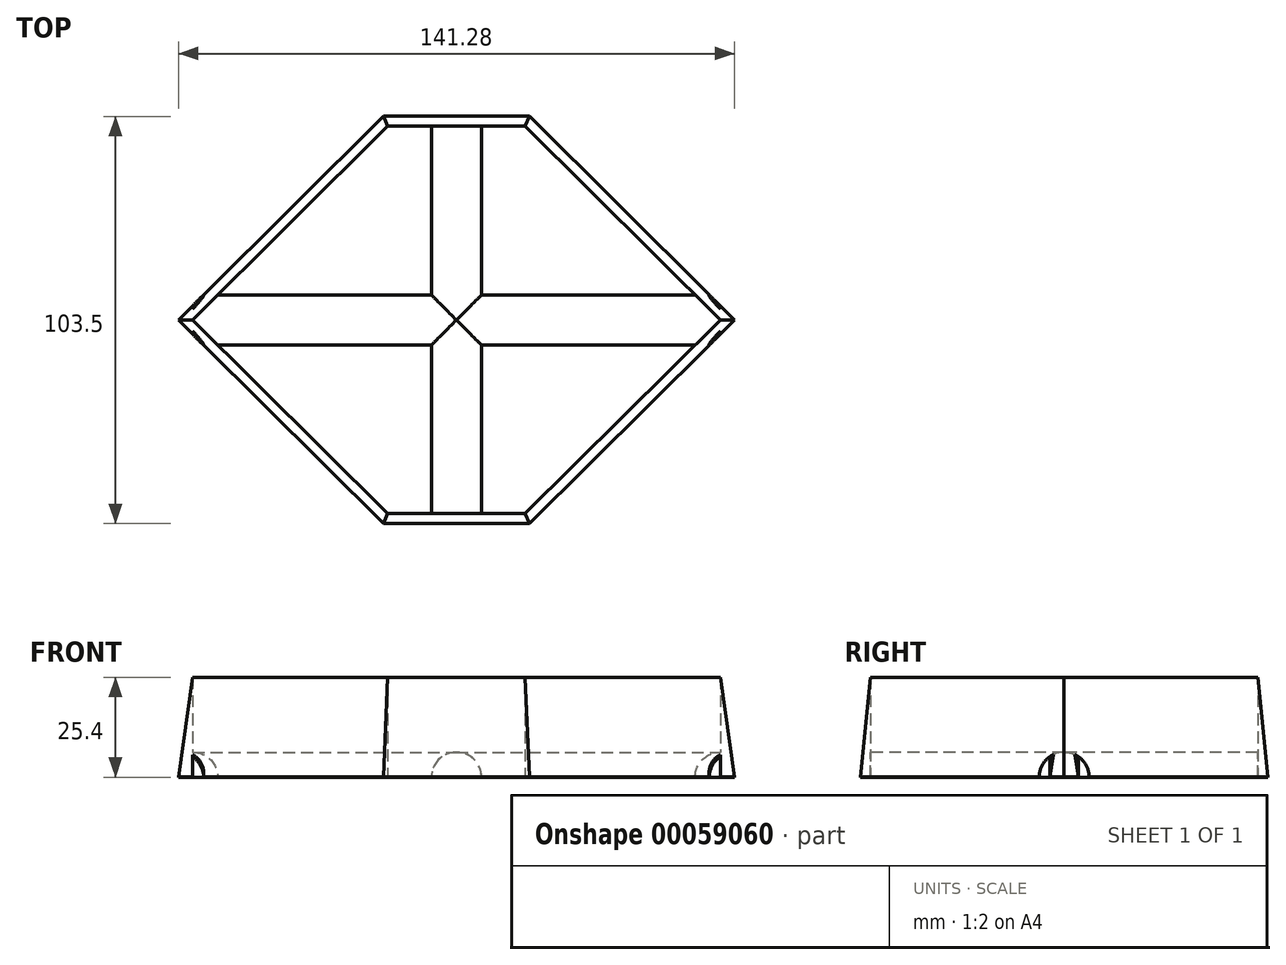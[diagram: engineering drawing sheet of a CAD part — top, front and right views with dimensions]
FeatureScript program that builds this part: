
annotation { "Feature Type Name" : "Feature", "Feature Type Description" : "" }
export const myFeature = defineFeature(function(context is Context, id is Id, definition is map)
    precondition{}
    {
        {
            var Q0;
            Q0=qCreatedBy(makeId("Top.planeOp"),FACE);
            var sketch = newSketch(context, id + "F0", { "sketchPlane" : qUnion([Q0])});
            skLineSegment(sketch, "E0", {"start": v(-67.03, 0) * mm, "end": v(-17.46, 49.21) * mm});
            skLineSegment(sketch, "E1", {"start": v(-17.46, 49.21) * mm, "end": v(17.46, 49.21) * mm});
            skLineSegment(sketch, "E2", {"start": v(17.46, 49.21) * mm, "end": v(67.03, 0) * mm});
            skLineSegment(sketch, "E3", {"start": v(-67.03, 0) * mm, "end": v(67.03, 0) * mm, "construction": true});
            skLineSegment(sketch, "E4.MirrorCS", {"start": v(-67.03, 0) * mm, "end": v(-17.46, -49.21) * mm});
            skLineSegment(sketch, "E5.MirrorCS", {"start": v(-17.46, -49.21) * mm, "end": v(17.46, -49.21) * mm});
            skLineSegment(sketch, "E6.MirrorCS", {"start": v(17.46, -49.21) * mm, "end": v(67.03, 0) * mm});
            skLineSegment(sketch, "E7.0", {"start": v(-70.64, 0) * mm, "end": v(-18.5, 51.75) * mm});
            skLineSegment(sketch, "E7.1", {"start": v(-18.5, -51.75) * mm, "end": v(18.5, -51.75) * mm});
            skLineSegment(sketch, "E7.2", {"start": v(18.5, -51.75) * mm, "end": v(70.64, 0) * mm});
            skLineSegment(sketch, "E7.3", {"start": v(-70.64, 0) * mm, "end": v(-18.5, -51.75) * mm});
            skLineSegment(sketch, "E7.4", {"start": v(18.5, 51.75) * mm, "end": v(70.64, 0) * mm});
            skLineSegment(sketch, "E7.5", {"start": v(-18.5, 51.75) * mm, "end": v(18.5, 51.75) * mm});
            skSolve(sketch);
        }
        {
            var Q0;
            Q0 = qSketchRegion(id + "F0", true);
            extrude(context, id + "F1", {"entities" : qUnion([Q0]), "depth" : 3 / 101.6 * mm, "offsetDistance" : 25.4 * mm});
        }
        {
            var Q0;
            Q0=makeQuery(id+"F1.opExtrude","CAP_FACE",FACE,{"disambiguationData":[OSD([sQuery(id+"F0.wireOp",EDGE,"E0"),sQuery(id+"F0.wireOp",EDGE,"E1"),sQuery(id+"F0.wireOp",EDGE,"E2"),sQuery(id+"F0.wireOp",EDGE,"E4.MirrorCS"),sQuery(id+"F0.wireOp",EDGE,"E5.MirrorCS"),sQuery(id+"F0.wireOp",EDGE,"E6.MirrorCS"),sQuery(id+"F0.wireOp",EDGE,"E7.0"),sQuery(id+"F0.wireOp",EDGE,"E7.1"),sQuery(id+"F0.wireOp",EDGE,"E7.2"),sQuery(id+"F0.wireOp",EDGE,"E7.3"),sQuery(id+"F0.wireOp",EDGE,"E7.4"),sQuery(id+"F0.wireOp",EDGE,"E7.5")])],"isStart":false});
            var sketch = newSketch(context, id + "F2", { "sketchPlane" : qUnion([Q0])});
            skLineSegment(sketch, "E8.0", {"start": v(-18.5, 51.75) * mm, "end": v(18.5, 51.75) * mm});
            skLineSegment(sketch, "E9.0", {"start": v(18.5, 51.75) * mm, "end": v(70.64, 0) * mm});
            skLineSegment(sketch, "E10.0", {"start": v(-70.64, 0) * mm, "end": v(-18.5, 51.75) * mm});
            skLineSegment(sketch, "E11.0", {"start": v(18.5, -51.75) * mm, "end": v(70.64, 0) * mm});
            skLineSegment(sketch, "E12.0", {"start": v(-18.5, -51.75) * mm, "end": v(18.5, -51.75) * mm});
            skLineSegment(sketch, "E13.0", {"start": v(-70.64, 0) * mm, "end": v(-18.5, -51.75) * mm});
            skSolve(sketch);
        }
        {
            var Q0;
            Q0=qCreatedBy(makeId("Top.planeOp"),FACE);
            cPlane(context, id + "F3", {"entities" : qUnion([Q0]), "cplaneType" : CPlaneType.OFFSET, "offset" : 25.4 * mm, "width" : 152.4 * mm, "height" : 152.4 * mm});
        }
        {
            var Q0;
            Q0=qCreatedBy(id+"F3.planeOp",FACE);
            var sketch = newSketch(context, id + "F4", { "sketchPlane" : qUnion([Q0])});
            skLineSegment(sketch, "E14.0", {"start": v(17.46, 49.21) * mm, "end": v(67.03, 0) * mm});
            skLineSegment(sketch, "E15.0", {"start": v(-17.46, 49.21) * mm, "end": v(17.46, 49.21) * mm});
            skLineSegment(sketch, "E16.0", {"start": v(-67.03, 0) * mm, "end": v(-17.46, 49.21) * mm});
            skLineSegment(sketch, "E17.0", {"start": v(-67.03, 0) * mm, "end": v(-17.46, -49.21) * mm});
            skLineSegment(sketch, "E18.0", {"start": v(-17.46, -49.21) * mm, "end": v(17.46, -49.21) * mm});
            skLineSegment(sketch, "E19.0", {"start": v(17.46, -49.21) * mm, "end": v(67.03, 0) * mm});
            skSolve(sketch);
        }
        {
            var Q0;
            Q0 = qSketchRegion(id + "F2", true);
            var Q1;
            Q1=makeQuery(id+"F4.imprint","IMPRINT",FACE,{"disambiguationData":[TD([[makeQuery(id+"F4.imprint","IMPRINT",EDGE,{"derivedFrom":sQuery(id+"F4.wireOp",EDGE,"E14.0")}),-1.0]])]});
            loft(context, id + "F5", {"operationType" : NewBodyOperationType.ADD, "sheetProfilesArray" : [{ "sheetProfileEntities" : qUnion([Q0]) }, { "sheetProfileEntities" : qUnion([Q1]) }]});
        }
        {
            var Q0;
            Q0=makeQuery(id+"F0.imprint","IMPRINT",FACE,{"disambiguationData":[TD([[makeQuery(id+"F0.imprint","IMPRINT",EDGE,{"derivedFrom":sQuery(id+"F0.wireOp",EDGE,"E0")}),-1.0]])]});
            extrude(context, id + "F6", {"entities" : qUnion([Q0]), "operationType" : NewBodyOperationType.REMOVE, "depth" : 25.4 * mm, "offsetDistance" : 25.4 * mm});
        }
        {
            var Q0;
            {var subQ0=sQuery(id+"F0.wireOp",EDGE,"E5.MirrorCS");Q0=makeQuery(id+"F6.boolean.opBoolean","MERGE",FACE,{"derivedFrom":[makeQuery(id+"F1.opExtrude","SWEPT_FACE",FACE,{"disambiguationData":[OSD([subQ0])]})],"fromTools":[makeQuery(id+"F6.opExtrude","SWEPT_FACE",FACE,{"disambiguationData":[OSD([subQ0])]})]});}
            var sketch = newSketch(context, id + "F7", { "sketchPlane" : qUnion([Q0])});
            skArc(sketch, "E20", {"start": v(6.35, 0) * mm, "mid": v(0, 6.35) * mm, "end": v(-6.35, 0) * mm});
            skSolve(sketch);
        }
        {
            var Q0;
            {var subQ0=sQuery(id+"F7.wireOp",EDGE,"E20");Q0=makeQuery(id+"F7.imprint","IMPRINT",FACE,{"disambiguationData":[TD([[makeQuery(id+"F7.imprint","IMPRINT",EDGE,{"derivedFrom":subQ0}),1.0]])]});}
            var Q1;
            {var subQ0=sQuery(id+"F0.wireOp",EDGE,"E1");Q1=makeQuery(id+"F6.boolean.opBoolean","MERGE",FACE,{"derivedFrom":[makeQuery(id+"F1.opExtrude","SWEPT_FACE",FACE,{"disambiguationData":[OSD([subQ0])]})],"fromTools":[makeQuery(id+"F6.opExtrude","SWEPT_FACE",FACE,{"disambiguationData":[OSD([subQ0])]})]});}
            extrude(context, id + "F8", {"entities" : qUnion([Q0]), "operationType" : NewBodyOperationType.ADD, "endBound" : BoundingType.UP_TO_SURFACE, "depth" : 25.4 * mm, "endBoundEntityFace" : qUnion([Q1]), "offsetDistance" : 25.4 * mm});
        }
        {
            var Q0;
            Q0=qCreatedBy(makeId("Right.planeOp"),FACE);
            var Q1;
            Q1=makeQuery(id+"F1.opExtrude","CAP_VERTEX",VERTEX,{"disambiguationData":[OSD([sQuery(id+"F0.wireOp",EDGE,"E2"),sQuery(id+"F0.wireOp",EDGE,"E6.MirrorCS")])],"isStart":true});
            cPlane(context, id + "F9", {"entities" : qUnion([Q0, Q1]), "cplaneType" : CPlaneType.PLANE_POINT, "offset" : 25.4 * mm, "width" : 152.4 * mm, "height" : 152.4 * mm});
        }
        {
            var Q0;
            Q0=qCreatedBy(id+"F9.planeOp",FACE);
            var sketch = newSketch(context, id + "F10", { "sketchPlane" : qUnion([Q0])});
            skArc(sketch, "E21", {"start": v(-6.35, 0) * mm, "mid": v(0, 6.35) * mm, "end": v(6.35, 0) * mm});
            skLineSegment(sketch, "E22", {"start": v(-6.35, 0) * mm, "end": v(6.35, 0) * mm});
            skSolve(sketch);
        }
        {
            var Q0;
            Q0 = qSketchRegion(id + "F10", true);
            var Q1;
            Q1=makeQuery(id+"F1.opExtrude","CAP_VERTEX",VERTEX,{"disambiguationData":[OSD([sQuery(id+"F0.wireOp",EDGE,"E0"),sQuery(id+"F0.wireOp",EDGE,"E4.MirrorCS")])],"isStart":true});
            extrude(context, id + "F11", {"entities" : qUnion([Q0]), "operationType" : NewBodyOperationType.ADD, "endBound" : BoundingType.UP_TO_VERTEX, "oppositeDirection" : true, "depth" : 25.4 * mm, "endBoundEntityVertex" : qUnion([Q1]), "offsetDistance" : 25.4 * mm});
        }
        {
            var Q0;
            {var subQ0=sQuery(id+"F10.wireOp",EDGE,"E21");var subQ2=sQuery(id+"F0.wireOp",EDGE,"E7.4");var subQ3=sQuery(id+"F10.wireOp",EDGE,"E22");Q0=makeQuery(id+"F11.boolean.opBoolean","SPLIT",FACE,{"disambiguationData":[TD([makeQuery(id+"F1.opExtrude","SWEPT_FACE",FACE,{"disambiguationData":[OSD([subQ2])]})])],"derivedFrom":makeQuery(id+"F11.opExtrude","CAP_FACE",FACE,{"disambiguationData":[OSD([subQ0,subQ3])],"isStart":true})});}
            var Q1;
            Q1=makeQuery(id+"F1.opExtrude","SWEPT_FACE",FACE,{"disambiguationData":[OSD([sQuery(id+"F0.wireOp",EDGE,"E7.4")])]});
            extrude(context, id + "F12", {"entities" : qUnion([Q0]), "operationType" : NewBodyOperationType.REMOVE, "endBound" : BoundingType.UP_TO_SURFACE, "oppositeDirection" : true, "depth" : 25.4 * mm, "endBoundEntityFace" : qUnion([Q1]), "offsetDistance" : 25.4 * mm});
        }
        {
            var Q0;
            {var subQ0=sQuery(id+"F10.wireOp",EDGE,"E21");var subQ2=sQuery(id+"F0.wireOp",EDGE,"E7.2");var subQ3=sQuery(id+"F10.wireOp",EDGE,"E22");Q0=makeQuery(id+"F11.boolean.opBoolean","SPLIT",FACE,{"disambiguationData":[TD([makeQuery(id+"F1.opExtrude","SWEPT_FACE",FACE,{"disambiguationData":[OSD([subQ2])]})])],"derivedFrom":makeQuery(id+"F11.opExtrude","CAP_FACE",FACE,{"disambiguationData":[OSD([subQ0,subQ3])],"isStart":true})});}
            var Q1;
            Q1=makeQuery(id+"F1.opExtrude","SWEPT_FACE",FACE,{"disambiguationData":[OSD([sQuery(id+"F0.wireOp",EDGE,"E7.2")])]});
            extrude(context, id + "F13", {"entities" : qUnion([Q0]), "operationType" : NewBodyOperationType.REMOVE, "endBound" : BoundingType.UP_TO_SURFACE, "oppositeDirection" : true, "depth" : 25.4 * mm, "endBoundEntityFace" : qUnion([Q1]), "offsetDistance" : 25.4 * mm});
        }
        {
            var Q0;
            {var subQ0=sQuery(id+"F10.wireOp",EDGE,"E21");var subQ2=sQuery(id+"F0.wireOp",EDGE,"E7.3");var subQ3=sQuery(id+"F10.wireOp",EDGE,"E22");Q0=makeQuery(id+"F11.boolean.opBoolean","SPLIT",FACE,{"disambiguationData":[TD([makeQuery(id+"F1.opExtrude","SWEPT_FACE",FACE,{"disambiguationData":[OSD([subQ2])]})])],"derivedFrom":makeQuery(id+"F11.opExtrude","CAP_FACE",FACE,{"disambiguationData":[OSD([subQ0,subQ3])],"isStart":false})});}
            var Q1;
            Q1=makeQuery(id+"F1.opExtrude","SWEPT_FACE",FACE,{"disambiguationData":[OSD([sQuery(id+"F0.wireOp",EDGE,"E7.3")])]});
            extrude(context, id + "F14", {"entities" : qUnion([Q0]), "operationType" : NewBodyOperationType.REMOVE, "endBound" : BoundingType.UP_TO_SURFACE, "oppositeDirection" : true, "depth" : 25.4 * mm, "endBoundEntityFace" : qUnion([Q1]), "offsetDistance" : 25.4 * mm});
        }
        {
            var Q0;
            {var subQ1=sQuery(id+"F10.wireOp",EDGE,"E21");var subQ2=sQuery(id+"F0.wireOp",EDGE,"E7.0");var subQ3=sQuery(id+"F10.wireOp",EDGE,"E22");Q0=makeQuery(id+"F11.boolean.opBoolean","SPLIT",FACE,{"disambiguationData":[TD([makeQuery(id+"F1.opExtrude","SWEPT_FACE",FACE,{"disambiguationData":[OSD([subQ2])]})])],"derivedFrom":makeQuery(id+"F11.opExtrude","CAP_FACE",FACE,{"disambiguationData":[OSD([subQ1,subQ3])],"isStart":false})});}
            var Q1;
            Q1=makeQuery(id+"F1.opExtrude","SWEPT_FACE",FACE,{"disambiguationData":[OSD([sQuery(id+"F0.wireOp",EDGE,"E7.0")])]});
            extrude(context, id + "F15", {"entities" : qUnion([Q0]), "operationType" : NewBodyOperationType.REMOVE, "endBound" : BoundingType.UP_TO_SURFACE, "oppositeDirection" : true, "depth" : 25.4 * mm, "endBoundEntityFace" : qUnion([Q1]), "offsetDistance" : 25.4 * mm});
        }
    });
